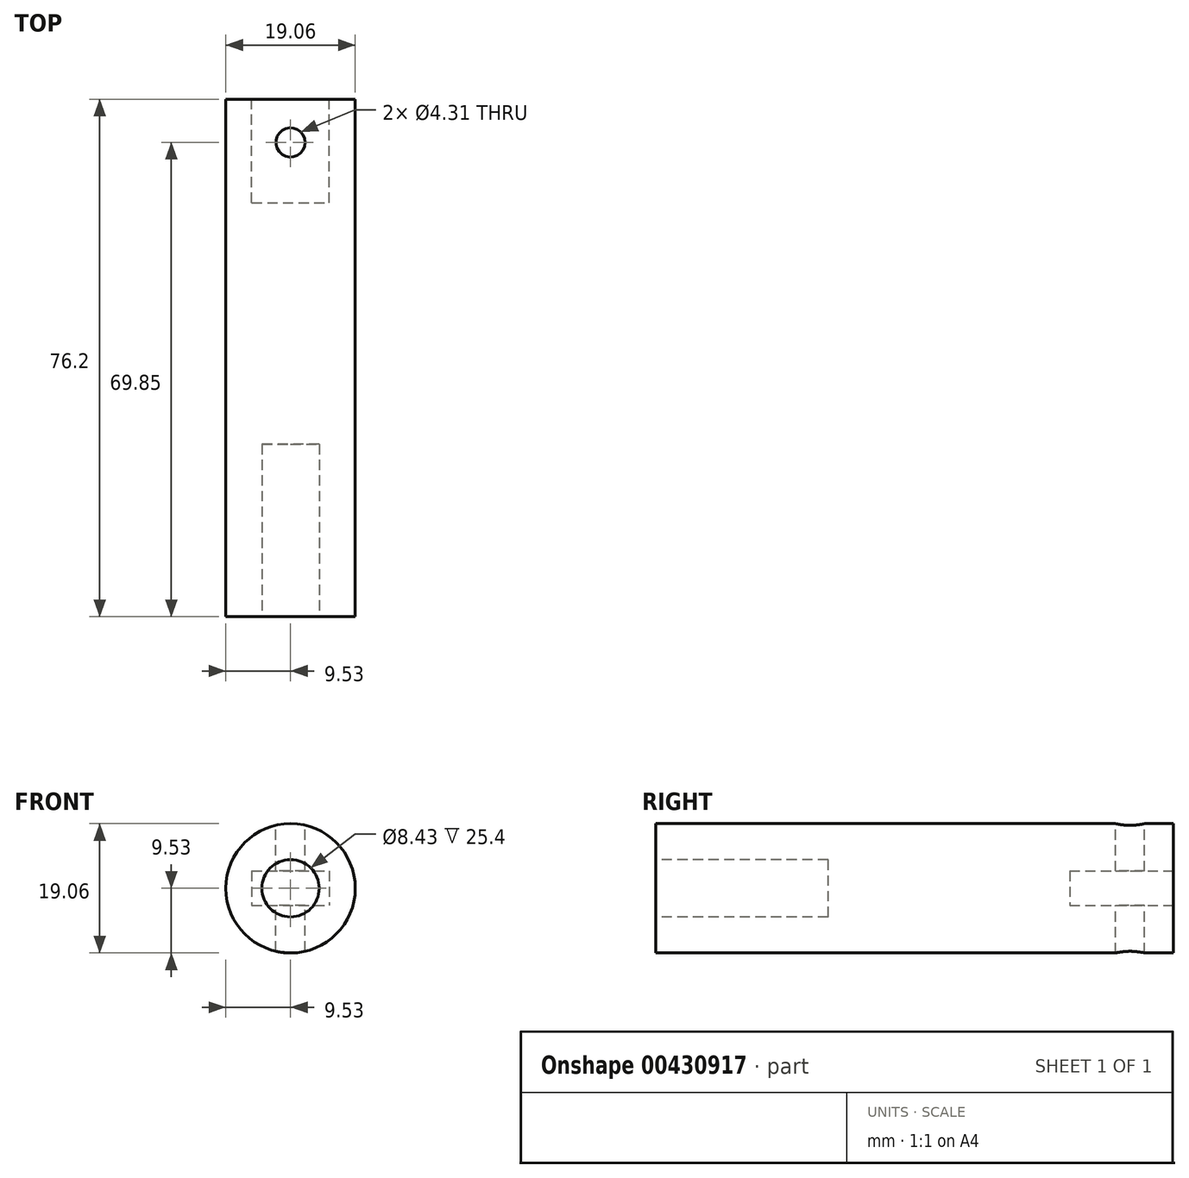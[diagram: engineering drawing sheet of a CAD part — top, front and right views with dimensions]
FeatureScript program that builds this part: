
annotation { "Feature Type Name" : "Feature", "Feature Type Description" : "" }
export const myFeature = defineFeature(function(context is Context, id is Id, definition is map)
    precondition{}
    {
        {
            var Q0;
            Q0=qCreatedBy(makeId("Front.planeOp"),FACE);
            var sketch = newSketch(context, id + "F0", { "sketchPlane" : qUnion([Q0])});
            skCircle(sketch, "E0", {"center": v(0, 0) * mm, "radius": 9.52 * mm});
            skSolve(sketch);
        }
        {
            var Q0;
            Q0=makeQuery(id+"F0.imprint","IMPRINT",FACE,{"disambiguationData":[TD([[makeQuery(id+"F0.imprint","IMPRINT",EDGE,{"derivedFrom":sQuery(id+"F0.wireOp",EDGE,"E0")}),1.0]])]});
            extrude(context, id + "F1", {"entities" : qUnion([Q0]), "oppositeDirection" : true, "depth" : 76.2 * mm});
        }
        {
            var Q0;
            Q0=makeQuery(id+"F1.opExtrude","CAP_FACE",FACE,{"disambiguationData":[OSD([sQuery(id+"F0.wireOp",EDGE,"E0")])],"isStart":false});
            var sketch = newSketch(context, id + "F2", { "sketchPlane" : qUnion([Q0])});
            skLineSegment(sketch, "E1.rect.bottom", {"start": v(5.71, 2.54) * mm, "end": v(-5.72, 2.54) * mm});
            skLineSegment(sketch, "E1.rect.top", {"start": v(5.72, -2.54) * mm, "end": v(-5.71, -2.54) * mm});
            skLineSegment(sketch, "E1.rect.left", {"start": v(5.71, 2.54) * mm, "end": v(5.72, -2.54) * mm});
            skLineSegment(sketch, "E1.rect.right", {"start": v(-5.72, 2.54) * mm, "end": v(-5.71, -2.54) * mm});
            skPoint(sketch, "E1.rect.middle", {"position": v(0, 0) * mm});
            skSolve(sketch);
        }
        {
            var Q0;
            Q0=makeQuery(id+"F2.imprint","IMPRINT",FACE,{"disambiguationData":[TD([[makeQuery(id+"F2.imprint","IMPRINT",EDGE,{"derivedFrom":sQuery(id+"F2.wireOp",EDGE,"E1.rect.bottom")}),1.0]])]});
            extrude(context, id + "F3", {"entities" : qUnion([Q0]), "operationType" : NewBodyOperationType.REMOVE, "oppositeDirection" : true, "depth" : 15.24 * mm});
        }
        {
            var Q0;
            Q0=qCreatedBy(makeId("Top.planeOp"),FACE);
            cPlane(context, id + "F4", {"entities" : qUnion([Q0]), "cplaneType" : CPlaneType.OFFSET, "offset" : 9.52 * mm, "width" : 152.4 * mm, "height" : 152.4 * mm});
        }
        {
            var Q0;
            Q0=qCreatedBy(id+"F4.planeOp",FACE);
            var sketch = newSketch(context, id + "F5", { "sketchPlane" : qUnion([Q0])});
            skCircle(sketch, "E2", {"center": v(0, 69.85) * mm, "radius": 2.15 * mm});
            skSolve(sketch);
        }
        {
            var Q0;
            Q0=makeQuery(id+"F5.imprint","IMPRINT",FACE,{"disambiguationData":[TD([[makeQuery(id+"F5.imprint","IMPRINT",EDGE,{"derivedFrom":sQuery(id+"F5.wireOp",EDGE,"E2")}),1.0]])]});
            extrude(context, id + "F6", {"entities" : qUnion([Q0]), "operationType" : NewBodyOperationType.REMOVE, "oppositeDirection" : true, "depth" : 25.4 * mm});
        }
        {
            var Q0;
            Q0=makeQuery(id+"F1.opExtrude","CAP_FACE",FACE,{"disambiguationData":[OSD([sQuery(id+"F0.wireOp",EDGE,"E0")])],"isStart":true});
            var sketch = newSketch(context, id + "F7", { "sketchPlane" : qUnion([Q0])});
            skCircle(sketch, "E3", {"center": v(0, 0) * mm, "radius": 4.22 * mm});
            skSolve(sketch);
        }
        {
            var Q0;
            Q0=makeQuery(id+"F7.imprint","IMPRINT",FACE,{"disambiguationData":[TD([[makeQuery(id+"F7.imprint","IMPRINT",EDGE,{"derivedFrom":sQuery(id+"F7.wireOp",EDGE,"E3")}),1.0]])]});
            extrude(context, id + "F8", {"entities" : qUnion([Q0]), "operationType" : NewBodyOperationType.REMOVE, "oppositeDirection" : true, "depth" : 25.4 * mm});
        }
    });
